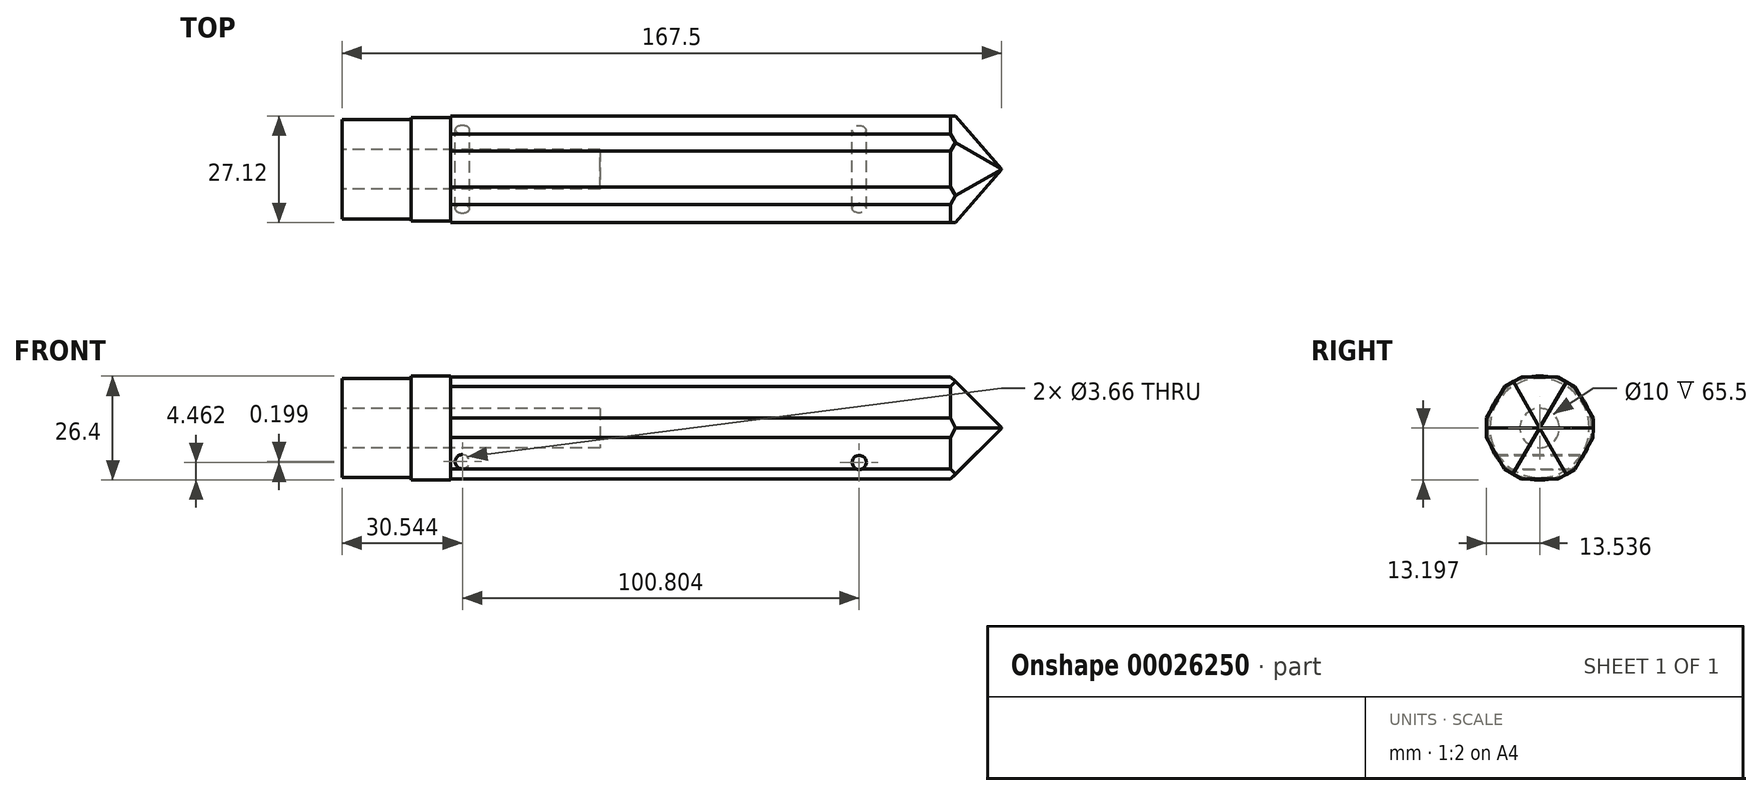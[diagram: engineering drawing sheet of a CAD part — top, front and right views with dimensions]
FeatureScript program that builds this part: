
annotation { "Feature Type Name" : "Feature", "Feature Type Description" : "" }
export const myFeature = defineFeature(function(context is Context, id is Id, definition is map)
    precondition{}
    {
        {
            var Q0;
            Q0=qCreatedBy(makeId("Front.planeOp"),FACE);
            var sketch = newSketch(context, id + "F0", { "sketchPlane" : qUnion([Q0])});
            skLineSegment(sketch, "E0.bottom", {"start": v(-84.2, -32.3) * mm, "end": v(45.8, -32.3) * mm});
            skLineSegment(sketch, "E0.top", {"start": v(-84.2, 37.7) * mm, "end": v(45.8, 37.7) * mm});
            skLineSegment(sketch, "E0.left", {"start": v(-84.2, -32.3) * mm, "end": v(-84.2, 37.7) * mm});
            skLineSegment(sketch, "E0.right", {"start": v(45.8, -32.3) * mm, "end": v(45.8, 37.7) * mm});
            skSolve(sketch);
        }
        {
            var Q0;
            Q0=makeQuery(id+"F0.imprint","IMPRINT",FACE,{"disambiguationData":[TD([[makeQuery(id+"F0.imprint","IMPRINT",EDGE,{"derivedFrom":sQuery(id+"F0.wireOp",EDGE,"E0.bottom")}),1.0]])]});
            extrude(context, id + "F1", {"entities" : qUnion([Q0]), "depth" : 40 * mm});
        }
        {
            var Q0;
            Q0=makeQuery(id+"F1.opExtrude","SWEPT_FACE",FACE,{"disambiguationData":[OSD([sQuery(id+"F0.wireOp",EDGE,"E0.left")])]});
            var sketch = newSketch(context, id + "F2", { "sketchPlane" : qUnion([Q0])});
            skCircle(sketch, "E1", {"center": v(20, 2.7) * mm, "radius": 5 * mm});
            skCircle(sketch, "E2", {"center": v(20, 2.7) * mm, "radius": 15 * mm});
            skCircle(sketch, "E3.cCircle", {"center": v(20, 2.7) * mm, "radius": 15 * mm, "construction": true});
            skLineSegment(sketch, "E3.0", {"start": v(27.46, 15.71) * mm, "end": v(35, 2.74) * mm});
            skLineSegment(sketch, "E3.1", {"start": v(35, 2.74) * mm, "end": v(27.54, -10.27) * mm});
            skLineSegment(sketch, "E3.2", {"start": v(27.54, -10.27) * mm, "end": v(12.54, -10.3) * mm});
            skLineSegment(sketch, "E3.3", {"start": v(12.54, -10.3) * mm, "end": v(5, 2.66) * mm});
            skLineSegment(sketch, "E3.4", {"start": v(5, 2.66) * mm, "end": v(12.46, 15.67) * mm});
            skLineSegment(sketch, "E3.5", {"start": v(12.46, 15.67) * mm, "end": v(27.46, 15.71) * mm});
            skSolve(sketch);
        }
        {
            var Q0;
            Q0=makeQuery(id+"F1.opExtrude","CAP_FACE",FACE,{"disambiguationData":[OSD([sQuery(id+"F0.wireOp",EDGE,"E0.bottom"),sQuery(id+"F0.wireOp",EDGE,"E0.top"),sQuery(id+"F0.wireOp",EDGE,"E0.left"),sQuery(id+"F0.wireOp",EDGE,"E0.right")])],"isStart":false});
            var sketch = newSketch(context, id + "F3", { "sketchPlane" : qUnion([Q0])});
            skCircle(sketch, "E4", {"center": v(-35.56, -24.64) * mm, "radius": 2 * mm});
            skCircle(sketch, "E5", {"center": v(174.33, -24.64) * mm, "radius": 2 * mm});
            skSolve(sketch);
        }
        {
            var Q0;
            Q0=makeQuery(id+"F3.imprint","IMPRINT",FACE,{"disambiguationData":[TD([[makeQuery(id+"F3.imprint","IMPRINT",EDGE,{"derivedFrom":sQuery(id+"F3.wireOp",EDGE,"E4")}),1.0]])]});
            var Q1;
            Q1=makeQuery(id+"F3.imprint","IMPRINT",FACE,{"disambiguationData":[TD([[makeQuery(id+"F3.imprint","IMPRINT",EDGE,{"derivedFrom":sQuery(id+"F3.wireOp",EDGE,"E5")}),1.0]])]});
            extrude(context, id + "F4", {"entities" : qUnion([Q0, Q1]), "operationType" : NewBodyOperationType.REMOVE, "endBound" : BoundingType.THROUGH_ALL, "oppositeDirection" : true, "depth" : 25 * mm});
        }
        {
            var Q0;
            {var subQ0=sQuery(id+"F0.wireOp",EDGE,"E0.left");Q0=makeQuery(id+"F2.imprint","IMPRINT",FACE,{"disambiguationData":[TD([[makeQuery(id+"F2.imprint","IMPRINT",EDGE,{"derivedFrom":makeQuery(id+"F1.opExtrude","CAP_EDGE",EDGE,{"disambiguationData":[OSD([subQ0])],"isStart":true})}),-1.0]])]});}
            extrude(context, id + "F5", {"entities" : qUnion([Q0]), "operationType" : NewBodyOperationType.REMOVE, "endBound" : BoundingType.THROUGH_ALL, "oppositeDirection" : true, "depth" : 25 * mm});
        }
        {
            var Q0;
            {var subQ0=sQuery(id+"F2.wireOp",EDGE,"E3.4");Q0=makeQuery(id+"F2.imprint","IMPRINT",FACE,{"disambiguationData":[TD([[makeQuery(id+"F2.imprint","IMPRINT",EDGE,{"derivedFrom":subQ0}),1.0]])]});}
            var Q1;
            {var subQ0=sQuery(id+"F2.wireOp",EDGE,"E3.5");Q1=makeQuery(id+"F2.imprint","IMPRINT",FACE,{"disambiguationData":[TD([[makeQuery(id+"F2.imprint","IMPRINT",EDGE,{"derivedFrom":subQ0}),1.0]])]});}
            var Q2;
            {var subQ0=sQuery(id+"F2.wireOp",EDGE,"E3.0");Q2=makeQuery(id+"F2.imprint","IMPRINT",FACE,{"disambiguationData":[TD([[makeQuery(id+"F2.imprint","IMPRINT",EDGE,{"derivedFrom":subQ0}),1.0]])]});}
            var Q3;
            {var subQ0=sQuery(id+"F2.wireOp",EDGE,"E3.1");Q3=makeQuery(id+"F2.imprint","IMPRINT",FACE,{"disambiguationData":[TD([[makeQuery(id+"F2.imprint","IMPRINT",EDGE,{"derivedFrom":subQ0}),1.0]])]});}
            var Q4;
            {var subQ0=sQuery(id+"F2.wireOp",EDGE,"E3.2");Q4=makeQuery(id+"F2.imprint","IMPRINT",FACE,{"disambiguationData":[TD([[makeQuery(id+"F2.imprint","IMPRINT",EDGE,{"derivedFrom":subQ0}),1.0]])]});}
            var Q5;
            {var subQ0=sQuery(id+"F2.wireOp",EDGE,"E3.3");Q5=makeQuery(id+"F2.imprint","IMPRINT",FACE,{"disambiguationData":[TD([[makeQuery(id+"F2.imprint","IMPRINT",EDGE,{"derivedFrom":subQ0}),1.0]])]});}
            extrude(context, id + "F6", {"entities" : qUnion([Q0, Q1, Q2, Q3, Q4, Q5]), "operationType" : NewBodyOperationType.REMOVE, "endBound" : BoundingType.THROUGH_ALL, "oppositeDirection" : true, "depth" : 25 * mm});
        }
        {
            var Q0;
            Q0=makeQuery(id+"F1.opExtrude","SWEPT_FACE",FACE,{"disambiguationData":[OSD([sQuery(id+"F0.wireOp",EDGE,"E0.right")])]});
            extrude(context, id + "F7", {"entities" : qUnion([Q0]), "operationType" : NewBodyOperationType.ADD, "depth" : 30 * mm});
        }
        {
            var Q0;
            Q0=makeQuery(id+"F7.opExtrude","CAP_EDGE",EDGE,{"disambiguationData":[OSD([sQuery(id+"F0.wireOp",EDGE,"E0.right"),sQuery(id+"F2.wireOp",EDGE,"E3.5")])],"isStart":false});
            var Q1;
            Q1=makeQuery(id+"F7.opExtrude","CAP_EDGE",EDGE,{"disambiguationData":[OSD([sQuery(id+"F0.wireOp",EDGE,"E0.right"),sQuery(id+"F2.wireOp",EDGE,"E3.0")])],"isStart":false});
            var Q2;
            Q2=makeQuery(id+"F7.opExtrude","CAP_EDGE",EDGE,{"disambiguationData":[OSD([sQuery(id+"F0.wireOp",EDGE,"E0.right"),sQuery(id+"F2.wireOp",EDGE,"E3.4")])],"isStart":false});
            var Q3;
            Q3=makeQuery(id+"F7.opExtrude","CAP_EDGE",EDGE,{"disambiguationData":[OSD([sQuery(id+"F0.wireOp",EDGE,"E0.right"),sQuery(id+"F2.wireOp",EDGE,"E3.3")])],"isStart":false});
            var Q4;
            Q4=makeQuery(id+"F7.opExtrude","CAP_EDGE",EDGE,{"disambiguationData":[OSD([sQuery(id+"F0.wireOp",EDGE,"E0.right"),sQuery(id+"F2.wireOp",EDGE,"E3.1")])],"isStart":false});
            var Q5;
            Q5=makeQuery(id+"F7.opExtrude","CAP_EDGE",EDGE,{"disambiguationData":[OSD([sQuery(id+"F0.wireOp",EDGE,"E0.right"),sQuery(id+"F2.wireOp",EDGE,"E3.2")])],"isStart":false});
            chamfer(context, id + "F8", {"entities" : qUnion([Q0, Q1, Q2, Q3, Q4, Q5]), "width" : 12.9 * mm, "tangentPropagation" : true});
        }
        {
            var Q0;
            {var subQ0=sQuery(id+"F2.wireOp",EDGE,"E2");var subQ1=sQuery(id+"F2.wireOp",EDGE,"E3.0");var subQ2=sQuery(id+"F2.wireOp",EDGE,"E3.5");Q0=makeQuery(id+"F7.boolean.opBoolean","MERGE",EDGE,{"derivedFrom":[makeQuery(id+"F6.boolean.opBoolean","TWEAK_EDGE",EDGE,{"derivedFrom":[makeQuery(id+"F6.opExtrude","SWEPT_EDGE",EDGE,{"disambiguationData":[OSD([subQ0,subQ1,subQ2]),ownerDisambiguation([makeQuery(id+"F6.opExtrude","SWEPT_BODY",BODY,{"disambiguationData":[OSD([subQ0,subQ1])]})])]}),makeQuery(id+"F6.opExtrude","SWEPT_EDGE",EDGE,{"disambiguationData":[OSD([subQ0,subQ1,subQ2]),ownerDisambiguation([makeQuery(id+"F6.opExtrude","SWEPT_BODY",BODY,{"disambiguationData":[OSD([subQ0,subQ2])]})])]})]}),makeQuery(id+"F7.opExtrude","SWEPT_EDGE",EDGE,{"disambiguationData":[OSD([sQuery(id+"F0.wireOp",EDGE,"E0.right"),subQ1,subQ2])]})]});}
            var Q1;
            {var subQ0=sQuery(id+"F2.wireOp",EDGE,"E2");var subQ1=sQuery(id+"F2.wireOp",EDGE,"E3.4");var subQ2=sQuery(id+"F2.wireOp",EDGE,"E3.5");Q1=makeQuery(id+"F7.boolean.opBoolean","MERGE",EDGE,{"derivedFrom":[makeQuery(id+"F6.boolean.opBoolean","TWEAK_EDGE",EDGE,{"derivedFrom":[makeQuery(id+"F6.opExtrude","SWEPT_EDGE",EDGE,{"disambiguationData":[OSD([subQ0,subQ1,subQ2]),ownerDisambiguation([makeQuery(id+"F6.opExtrude","SWEPT_BODY",BODY,{"disambiguationData":[OSD([subQ0,subQ2])]})])]}),makeQuery(id+"F6.opExtrude","SWEPT_EDGE",EDGE,{"disambiguationData":[OSD([subQ0,subQ1,subQ2]),ownerDisambiguation([makeQuery(id+"F6.opExtrude","SWEPT_BODY",BODY,{"disambiguationData":[OSD([subQ0,subQ1])]})])]})]}),makeQuery(id+"F7.opExtrude","SWEPT_EDGE",EDGE,{"disambiguationData":[OSD([sQuery(id+"F0.wireOp",EDGE,"E0.right"),subQ1,subQ2])]})]});}
            var Q2;
            {var subQ0=sQuery(id+"F2.wireOp",EDGE,"E2");var subQ1=sQuery(id+"F2.wireOp",EDGE,"E3.0");var subQ2=sQuery(id+"F2.wireOp",EDGE,"E3.1");Q2=makeQuery(id+"F7.boolean.opBoolean","MERGE",EDGE,{"derivedFrom":[makeQuery(id+"F6.boolean.opBoolean","TWEAK_EDGE",EDGE,{"derivedFrom":[makeQuery(id+"F6.opExtrude","SWEPT_EDGE",EDGE,{"disambiguationData":[OSD([subQ0,subQ1,subQ2]),ownerDisambiguation([makeQuery(id+"F6.opExtrude","SWEPT_BODY",BODY,{"disambiguationData":[OSD([subQ0,subQ1])]})])]}),makeQuery(id+"F6.opExtrude","SWEPT_EDGE",EDGE,{"disambiguationData":[OSD([subQ0,subQ1,subQ2]),ownerDisambiguation([makeQuery(id+"F6.opExtrude","SWEPT_BODY",BODY,{"disambiguationData":[OSD([subQ0,subQ2])]})])]})]}),makeQuery(id+"F7.opExtrude","SWEPT_EDGE",EDGE,{"disambiguationData":[OSD([sQuery(id+"F0.wireOp",EDGE,"E0.right"),subQ1,subQ2])]})]});}
            var Q3;
            {var subQ0=sQuery(id+"F2.wireOp",EDGE,"E2");var subQ1=sQuery(id+"F2.wireOp",EDGE,"E3.1");var subQ2=sQuery(id+"F2.wireOp",EDGE,"E3.2");Q3=makeQuery(id+"F7.boolean.opBoolean","MERGE",EDGE,{"derivedFrom":[makeQuery(id+"F6.boolean.opBoolean","TWEAK_EDGE",EDGE,{"derivedFrom":[makeQuery(id+"F6.opExtrude","SWEPT_EDGE",EDGE,{"disambiguationData":[OSD([subQ0,subQ1,subQ2]),ownerDisambiguation([makeQuery(id+"F6.opExtrude","SWEPT_BODY",BODY,{"disambiguationData":[OSD([subQ0,subQ2])]})])]}),makeQuery(id+"F6.opExtrude","SWEPT_EDGE",EDGE,{"disambiguationData":[OSD([subQ0,subQ1,subQ2]),ownerDisambiguation([makeQuery(id+"F6.opExtrude","SWEPT_BODY",BODY,{"disambiguationData":[OSD([subQ0,subQ1])]})])]})]}),makeQuery(id+"F7.opExtrude","SWEPT_EDGE",EDGE,{"disambiguationData":[OSD([sQuery(id+"F0.wireOp",EDGE,"E0.right"),subQ1,subQ2])]})]});}
            var Q4;
            {var subQ0=sQuery(id+"F2.wireOp",EDGE,"E2");var subQ1=sQuery(id+"F2.wireOp",EDGE,"E3.3");var subQ2=sQuery(id+"F2.wireOp",EDGE,"E3.4");Q4=makeQuery(id+"F7.boolean.opBoolean","MERGE",EDGE,{"derivedFrom":[makeQuery(id+"F6.boolean.opBoolean","TWEAK_EDGE",EDGE,{"derivedFrom":[makeQuery(id+"F6.opExtrude","SWEPT_EDGE",EDGE,{"disambiguationData":[OSD([subQ0,subQ1,subQ2]),ownerDisambiguation([makeQuery(id+"F6.opExtrude","SWEPT_BODY",BODY,{"disambiguationData":[OSD([subQ0,subQ2])]})])]}),makeQuery(id+"F6.opExtrude","SWEPT_EDGE",EDGE,{"disambiguationData":[OSD([subQ0,subQ1,subQ2]),ownerDisambiguation([makeQuery(id+"F6.opExtrude","SWEPT_BODY",BODY,{"disambiguationData":[OSD([subQ0,subQ1])]})])]})]}),makeQuery(id+"F7.opExtrude","SWEPT_EDGE",EDGE,{"disambiguationData":[OSD([sQuery(id+"F0.wireOp",EDGE,"E0.right"),subQ1,subQ2])]})]});}
            var Q5;
            {var subQ0=sQuery(id+"F2.wireOp",EDGE,"E2");var subQ1=sQuery(id+"F2.wireOp",EDGE,"E3.2");var subQ2=sQuery(id+"F2.wireOp",EDGE,"E3.3");Q5=makeQuery(id+"F7.boolean.opBoolean","MERGE",EDGE,{"derivedFrom":[makeQuery(id+"F6.boolean.opBoolean","TWEAK_EDGE",EDGE,{"derivedFrom":[makeQuery(id+"F6.opExtrude","SWEPT_EDGE",EDGE,{"disambiguationData":[OSD([subQ0,subQ1,subQ2]),ownerDisambiguation([makeQuery(id+"F6.opExtrude","SWEPT_BODY",BODY,{"disambiguationData":[OSD([subQ0,subQ2])]})])]}),makeQuery(id+"F6.opExtrude","SWEPT_EDGE",EDGE,{"disambiguationData":[OSD([subQ0,subQ1,subQ2]),ownerDisambiguation([makeQuery(id+"F6.opExtrude","SWEPT_BODY",BODY,{"disambiguationData":[OSD([subQ0,subQ1])]})])]})]}),makeQuery(id+"F7.opExtrude","SWEPT_EDGE",EDGE,{"disambiguationData":[OSD([sQuery(id+"F0.wireOp",EDGE,"E0.right"),subQ1,subQ2])]})]});}
            chamfer(context, id + "F9", {"entities" : qUnion([Q0, Q1, Q2, Q3, Q4, Q5]), "width" : 5 * mm, "tangentPropagation" : true});
        }
        {
            var Q0;
            Q0=qCreatedBy(makeId("Front.planeOp"),FACE);
            var sketch = newSketch(context, id + "F10", { "sketchPlane" : qUnion([Q0])});
            skCircle(sketch, "E6", {"center": v(-61.16, -5.86) * mm, "radius": 1.83 * mm});
            skCircle(sketch, "E7", {"center": v(39.65, -6.06) * mm, "radius": 1.83 * mm});
            skSolve(sketch);
        }
        {
            var Q0;
            Q0=makeQuery(id+"F10.imprint","IMPRINT",FACE,{"disambiguationData":[TD([[makeQuery(id+"F10.imprint","IMPRINT",EDGE,{"derivedFrom":sQuery(id+"F10.wireOp",EDGE,"E7")}),1.0]])]});
            var Q1;
            Q1=makeQuery(id+"F10.imprint","IMPRINT",FACE,{"disambiguationData":[TD([[makeQuery(id+"F10.imprint","IMPRINT",EDGE,{"derivedFrom":sQuery(id+"F10.wireOp",EDGE,"E6")}),1.0]])]});
            extrude(context, id + "F11", {"entities" : qUnion([Q0, Q1]), "operationType" : NewBodyOperationType.REMOVE, "endBound" : BoundingType.THROUGH_ALL, "depth" : 25 * mm});
        }
        {
            var Q0;
            Q0=makeQuery(id+"F1.opExtrude","SWEPT_FACE",FACE,{"disambiguationData":[OSD([sQuery(id+"F0.wireOp",EDGE,"E0.left")])]});
            extrude(context, id + "F12", {"entities" : qUnion([Q0]), "operationType" : NewBodyOperationType.REMOVE, "oppositeDirection" : true, "depth" : 20 * mm});
        }
        {
            var Q0;
            Q0=makeQuery(id+"F12.boolean.opBoolean","COPY",FACE,{"derivedFrom":makeQuery(id+"F12.opExtrude","CAP_FACE",FACE,{"disambiguationData":[OSD([sQuery(id+"F0.wireOp",EDGE,"E0.left")])],"isStart":false})});
            var sketch = newSketch(context, id + "F13", { "sketchPlane" : qUnion([Q0])});
            skPoint(sketch, "E8", {"position": v(20.02, 2.68) * mm});
            skCircle(sketch, "E9", {"center": v(20.02, 2.68) * mm, "radius": 13.2 * mm});
            skSolve(sketch);
        }
        {
            var Q0;
            Q0 = qSketchRegion(id + "F13", true);
            extrude(context, id + "F14", {"entities" : qUnion([Q0]), "operationType" : NewBodyOperationType.ADD, "depth" : 10 * mm});
        }
        {
            var Q0;
            Q0=makeQuery(id+"F14.opExtrude","CAP_FACE",FACE,{"disambiguationData":[OSD([sQuery(id+"F13.wireOp",EDGE,"E9")])],"isStart":false});
            var sketch = newSketch(context, id + "F15", { "sketchPlane" : qUnion([Q0])});
            skCircle(sketch, "E10", {"center": v(20.02, 2.68) * mm, "radius": 12.6 * mm});
            skSolve(sketch);
        }
        {
            var Q0;
            Q0 = qSketchRegion(id + "F15", true);
            extrude(context, id + "F16", {"entities" : qUnion([Q0]), "operationType" : NewBodyOperationType.ADD, "depth" : 17.5 * mm});
        }
        {
            var Q0;
            Q0=makeQuery(id+"F16.opExtrude","CAP_FACE",FACE,{"disambiguationData":[OSD([sQuery(id+"F15.wireOp",EDGE,"E10")])],"isStart":false});
            var sketch = newSketch(context, id + "F17", { "sketchPlane" : qUnion([Q0])});
            skCircle(sketch, "E11", {"center": v(20.02, 2.68) * mm, "radius": 5 * mm});
            skSolve(sketch);
        }
        {
            var Q0;
            Q0=makeQuery(id+"F17.imprint","IMPRINT",FACE,{"disambiguationData":[TD([[makeQuery(id+"F17.imprint","IMPRINT",EDGE,{"derivedFrom":sQuery(id+"F17.wireOp",EDGE,"E11")}),1.0]])]});
            extrude(context, id + "F18", {"entities" : qUnion([Q0]), "operationType" : NewBodyOperationType.REMOVE, "oppositeDirection" : true, "depth" : 65.5 * mm});
        }
    });
